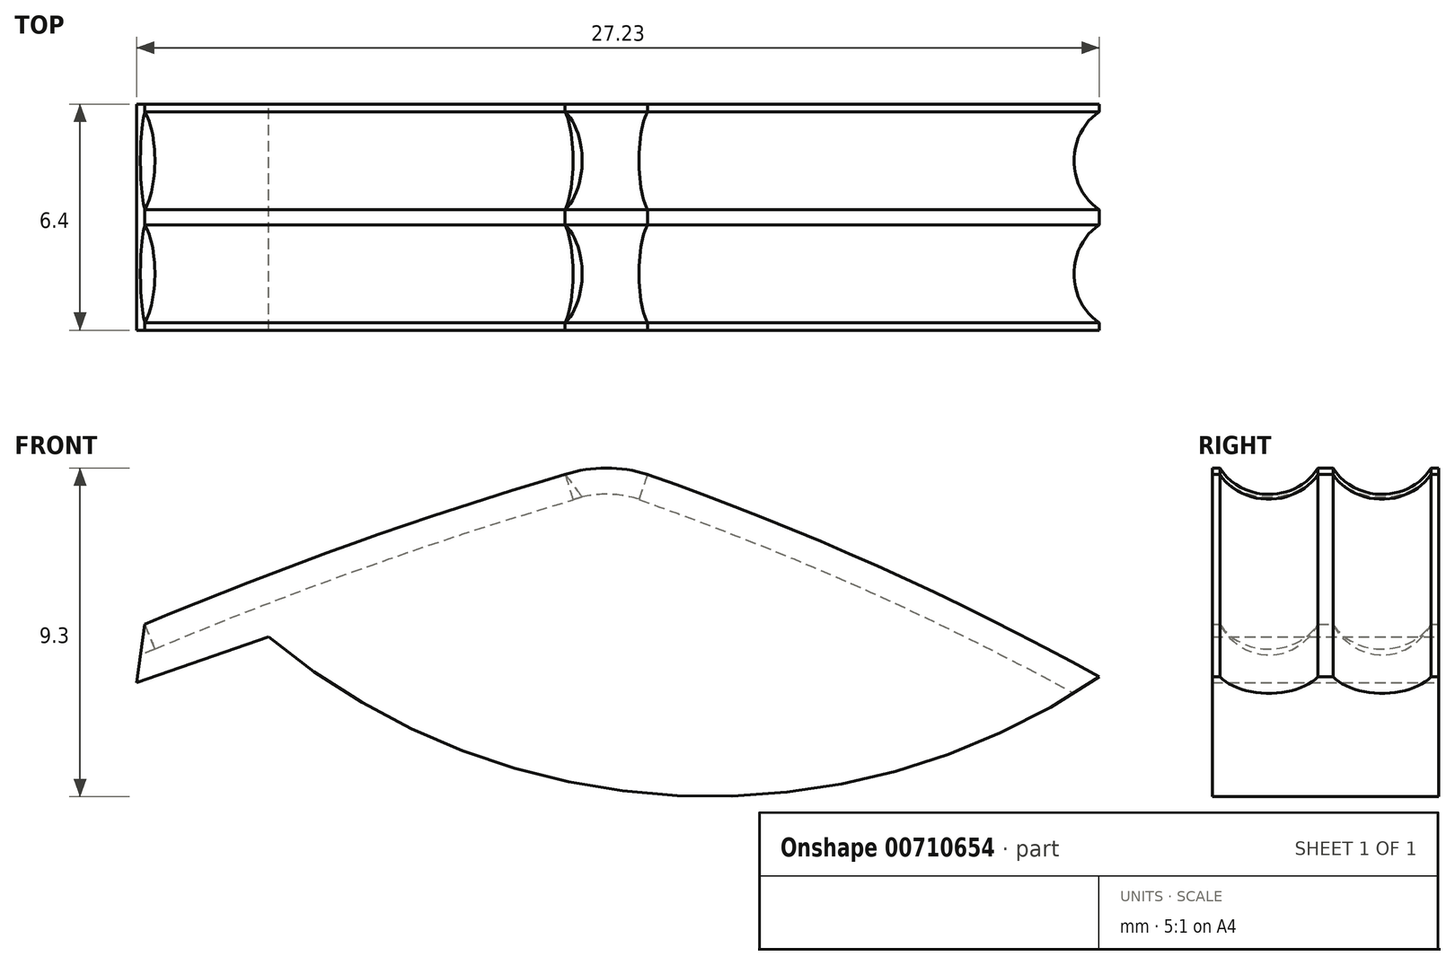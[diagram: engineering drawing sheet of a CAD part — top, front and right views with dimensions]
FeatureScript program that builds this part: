
annotation { "Feature Type Name" : "Feature", "Feature Type Description" : "" }
export const myFeature = defineFeature(function(context is Context, id is Id, definition is map)
    precondition{}
    {
        {
            var Q0;
            Q0=qCreatedBy(makeId("Front.planeOp"),FACE);
            var sketch = newSketch(context, id + "F0", { "sketchPlane" : qUnion([Q0])});
            skArc(sketch, "E0", {"start": v(-10.72, 1.13) * mm, "mid": v(0.84, -3.36) * mm, "end": v(12.78, 0) * mm});
            skArc(sketch, "E1", {"start": v(12.78, 0) * mm, "mid": v(6.51, 3.13) * mm, "end": v(0, 5.73) * mm});
            skArc(sketch, "E2", {"start": v(0, 5.73) * mm, "mid": v(-1.16, 5.91) * mm, "end": v(-2.33, 5.73) * mm});
            skArc(sketch, "E3", {"start": v(-2.33, 5.73) * mm, "mid": v(-8.33, 3.77) * mm, "end": v(-14.22, 1.49) * mm});
            skLineSegment(sketch, "E4", {"start": v(-10.72, 1.13) * mm, "end": v(-14.45, -0.16) * mm});
            skLineSegment(sketch, "E5", {"start": v(-14.45, -0.16) * mm, "end": v(-14.22, 1.49) * mm});
            skLineSegment(sketch, "E6", {"start": v(-14.92, 1.2) * mm, "end": v(-14.22, 1.49) * mm});
            skLineSegment(sketch, "E7", {"start": v(-14.92, 1.2) * mm, "end": v(-14.45, -0.16) * mm});
            skSolve(sketch);
        }
        {
            var Q0;
            Q0=makeQuery(id+"F0.imprint","IMPRINT",FACE,{"disambiguationData":[TD([[makeQuery(id+"F0.imprint","IMPRINT",EDGE,{"derivedFrom":sQuery(id+"F0.wireOp",EDGE,"E0")}),1.0]])]});
            extrude(context, id + "F1", {"entities" : qUnion([Q0]), "endBound" : BoundingType.SYMMETRIC, "depth" : 6.4 * mm, "offsetDistance" : 25 * mm});
        }
        {
            var Q0;
            Q0=qCreatedBy(makeId("Right.planeOp"),FACE);
            var sketch = newSketch(context, id + "F2", { "sketchPlane" : qUnion([Q0])});
            skCircle(sketch, "E8", {"center": v(1.6, 6.53) * mm, "radius": 1.6 * mm});
            skCircle(sketch, "E9", {"center": v(-1.6, 6.53) * mm, "radius": 1.6 * mm});
            skSolve(sketch);
        }
        {
            var Q0;
            Q0=makeQuery(id+"F2.imprint","IMPRINT",FACE,{"disambiguationData":[TD([[makeQuery(id+"F2.imprint","IMPRINT",EDGE,{"derivedFrom":sQuery(id+"F2.wireOp",EDGE,"E9")}),1.0]])]});
            var Q1;
            Q1=makeQuery(id+"F2.imprint","IMPRINT",FACE,{"disambiguationData":[TD([[makeQuery(id+"F2.imprint","IMPRINT",EDGE,{"derivedFrom":sQuery(id+"F2.wireOp",EDGE,"E8")}),1.0]])]});
            var Q2;
            Q2=sQuery(id+"F0.wireOp",EDGE,"E3");
            var Q3;
            Q3=sQuery(id+"F0.wireOp",EDGE,"E2");
            var Q4;
            Q4=sQuery(id+"F0.wireOp",EDGE,"E1");
            var Q5;
            Q5=sQuery(id+"F0.wireOp",EDGE,"E6");
            sweep(context, id + "F3", {"operationType" : NewBodyOperationType.REMOVE, "profiles" : qUnion([Q0, Q1]), "path" : qUnion([Q2, Q3, Q4, Q5])});
        }
    });
